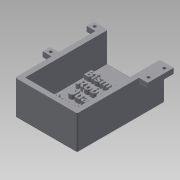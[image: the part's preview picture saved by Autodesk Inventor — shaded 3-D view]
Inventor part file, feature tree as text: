
AUTODESK INVENTOR PART (.ipt)
format: ipt  version: 2015 SP1 (Build 190203100, 203)  size: 1,043,968 bytes
history: native  units: mm
features: sketch x13, extrude x12, projected_geometry x9, fillet x2, reference x2
ambient origin geometry x8: Origin, YZ Plane, XZ Plane, XY Plane, X Axis, Y Axis, Z Axis, Center Point
bodies: Solid1 (feature_tree)
feature tree (38):
  extrude  "Extrusion1"  Depth=60.0mm
  extrude  "Extrusion3"  Depth=3.5mm TaperAngle=0.0deg
  extrude  "Extrusion4"  Depth=3.5mm TaperAngle=0.0deg
  extrude  "Extrusion5"  Depth=3.5mm TaperAngle=0.0deg
  extrude  "Extrusion6"  Depth=6.0mm
  extrude  "Extrusion7"  Depth=3.5mm
  extrude  "Extrusion8"  Depth=2.0mm
  fillet  "Fillet1"  Radius=2.0mm
  extrude  "Extrusion9"  Depth=3.5mm TaperAngle=0.0deg
  extrude  "Extrusion10"  Depth=3.5mm TaperAngle=0.0deg
  fillet  "Fillet2"  Radius=3.5mm
  extrude  "Extrusion11"  Depth=3.5mm TaperAngle=0.0deg
  extrude  "Extrusion12"  TaperAngle=45.0deg  [1 undecoded]
  sketch  "Sketch17"  dims[d63=3.0mm d64=0.0mm]
  extrude  "Extrusion14"  [1 undecoded]
  sketch  "Sketch1"  dims[d0=42.5mm d1=60.0mm]
  sketch  "Sketch4"  dims[d2=3.5mm d3=0.0mm d11=20.0mm d12=0.0mm]
  sketch  "Sketch5"  dims[d13=3.5mm d14=0.0mm d15=3.5mm d16=0.0mm]
  sketch  "Sketch6"  dims[d17=3.5mm d18=0.0mm d19=3.5mm d20=0.0mm]
  sketch  "Sketch7"  dims[d21=6.0mm d22=6.0mm]
  reference  "Reference1"
  sketch  "Sketch8"  dims[d23=3.5mm d24=2.0mm]
  reference  "Reference2"
  sketch  "Sketch11"  dims[d25=2.0mm d26=2.0mm d27=2.0mm]
  projected_geometry  "Projected Loop1"
  projected_geometry  "Projected Loop2"
  projected_geometry  "Projected Loop3"
  sketch  "Sketch12"  dims[d28=3.5mm d29=3.5mm d30=0.0mm]
  sketch  "Sketch13"  dims[d31=1.0mm d32=3.5mm d33=0.0mm d34=3.5mm d35=0.0mm]
  projected_geometry  "Projected Loop4"
  projected_geometry  "Projected Loop5"
  projected_geometry  "Projected Loop6"
  projected_geometry  "Projected Loop7"
  projected_geometry  "Projected Loop8"
  sketch  "Sketch15"  dims[d36=1.0mm d51=3.5mm d52=0.0mm]
  projected_geometry  "Projected Loop9"
  sketch  "Sketch16"  dims[d53=3.5mm d54=0.0mm d57=45.0deg d58=45.0deg d59=135.0deg d60=135.0deg]
  sketch  "Sketch19"
note: 2 required parameter values undecoded (feature->parameter linkage not recoverable at this tier; creation-order binding heuristic only, values carry confidence <= 0.55)
